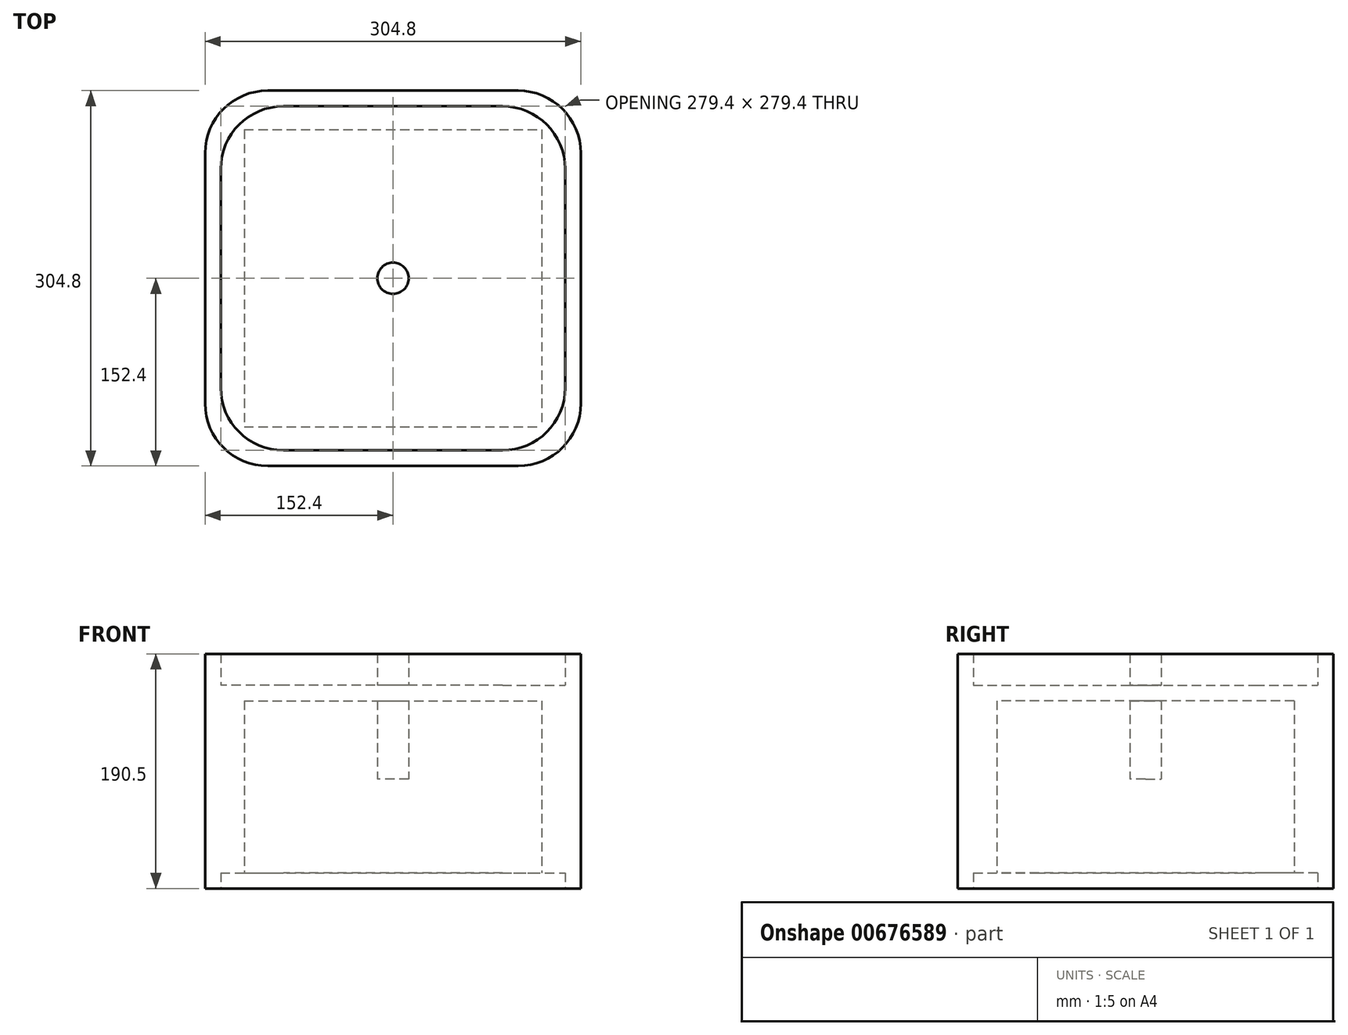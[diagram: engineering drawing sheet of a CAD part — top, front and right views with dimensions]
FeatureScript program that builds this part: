
annotation { "Feature Type Name" : "Feature", "Feature Type Description" : "" }
export const myFeature = defineFeature(function(context is Context, id is Id, definition is map)
    precondition{}
    {
        {
            var Q0;
            Q0=qCreatedBy(makeId("Top.planeOp"),FACE);
            var sketch = newSketch(context, id + "F0", { "sketchPlane" : qUnion([Q0])});
            skPoint(sketch, "E0.middle", {"position": v(0, 0) * mm});
            skLineSegment(sketch, "E1.bottom", {"start": v(139.7, -139.7) * mm, "end": v(-139.7, -139.7) * mm});
            skLineSegment(sketch, "E1.top", {"start": v(139.7, 139.7) * mm, "end": v(-139.7, 139.7) * mm});
            skLineSegment(sketch, "E1.left", {"start": v(139.7, -139.7) * mm, "end": v(139.7, 139.7) * mm});
            skLineSegment(sketch, "E1.right", {"start": v(-139.7, -139.7) * mm, "end": v(-139.7, 139.7) * mm});
            skCircle(sketch, "E2", {"center": v(0, 0) * mm, "radius": 12.7 * mm});
            skLineSegment(sketch, "E3.bottom", {"start": v(152.4, -152.4) * mm, "end": v(-152.4, -152.4) * mm});
            skLineSegment(sketch, "E3.top", {"start": v(152.4, 152.4) * mm, "end": v(-152.4, 152.4) * mm});
            skLineSegment(sketch, "E3.left", {"start": v(152.4, -152.4) * mm, "end": v(152.4, 152.4) * mm});
            skLineSegment(sketch, "E3.right", {"start": v(-152.4, -152.4) * mm, "end": v(-152.4, 152.4) * mm});
            skSolve(sketch);
        }
        {
            var Q0;
            Q0=makeQuery(id+"F0.imprint","IMPRINT",FACE,{"disambiguationData":[TD([[makeQuery(id+"F0.imprint","IMPRINT",EDGE,{"derivedFrom":sQuery(id+"F0.wireOp",EDGE,"E1.bottom")}),-1.0]])]});
            extrude(context, id + "F1", {"entities" : qUnion([Q0]), "endBound" : BoundingType.SYMMETRIC, "depth" : 152.4 * mm, "offsetDistance" : 25.4 * mm});
        }
        {
            var Q0;
            Q0=makeQuery(id+"F0.imprint","IMPRINT",FACE,{"disambiguationData":[TD([[makeQuery(id+"F0.imprint","IMPRINT",EDGE,{"derivedFrom":sQuery(id+"F0.wireOp",EDGE,"E1.bottom")}),1.0]])]});
            extrude(context, id + "F2", {"entities" : qUnion([Q0]), "operationType" : NewBodyOperationType.ADD, "depth" : 101.6 * mm, "offsetDistance" : 25.4 * mm, "hasSecondDirection" : true, "secondDirectionOppositeDirection" : true, "secondDirectionDepth" : 88.9 * mm});
        }
        {
            var Q0;
            Q0=makeQuery(id+"F2.opExtrude","SWEPT_EDGE",EDGE,{"disambiguationData":[OSD([sQuery(id+"F0.wireOp",EDGE,"E3.bottom"),sQuery(id+"F0.wireOp",EDGE,"E3.left")])]});
            var Q1;
            Q1=makeQuery(id+"F2.opExtrude","SWEPT_EDGE",EDGE,{"disambiguationData":[OSD([sQuery(id+"F0.wireOp",EDGE,"E3.top"),sQuery(id+"F0.wireOp",EDGE,"E3.left")])]});
            var Q2;
            Q2=makeQuery(id+"F2.opExtrude","SWEPT_EDGE",EDGE,{"disambiguationData":[OSD([sQuery(id+"F0.wireOp",EDGE,"E3.top"),sQuery(id+"F0.wireOp",EDGE,"E3.right")])]});
            var Q3;
            Q3=makeQuery(id+"F2.opExtrude","SWEPT_EDGE",EDGE,{"disambiguationData":[OSD([sQuery(id+"F0.wireOp",EDGE,"E3.bottom"),sQuery(id+"F0.wireOp",EDGE,"E3.right")])]});
            var Q4;
            {var subQ0=sQuery(id+"F0.wireOp",EDGE,"E1.right");var subQ1=sQuery(id+"F0.wireOp",EDGE,"E1.left");var subQ2=sQuery(id+"F0.wireOp",EDGE,"E1.top");var subQ3=sQuery(id+"F0.wireOp",EDGE,"E1.bottom");Q4=makeQuery(id+"F2.boolean.opBoolean","SPLIT",EDGE,{"disambiguationData":[TD([makeQuery(id+"F1.opExtrude","CAP_FACE",FACE,{"disambiguationData":[OSD([subQ3,subQ2,subQ1,subQ0,sQuery(id+"F0.wireOp",EDGE,"E2")])],"isStart":false})])],"derivedFrom":makeQuery(id+"F2.opExtrude","SWEPT_EDGE",EDGE,{"disambiguationData":[OSD([subQ3,subQ0])]})});}
            var Q5;
            {var subQ0=sQuery(id+"F0.wireOp",EDGE,"E1.right");var subQ1=sQuery(id+"F0.wireOp",EDGE,"E1.left");var subQ2=sQuery(id+"F0.wireOp",EDGE,"E1.top");var subQ3=sQuery(id+"F0.wireOp",EDGE,"E1.bottom");Q5=makeQuery(id+"F2.boolean.opBoolean","SPLIT",EDGE,{"disambiguationData":[TD([makeQuery(id+"F1.opExtrude","CAP_FACE",FACE,{"disambiguationData":[OSD([subQ3,subQ2,subQ1,subQ0,sQuery(id+"F0.wireOp",EDGE,"E2")])],"isStart":false})])],"derivedFrom":makeQuery(id+"F2.opExtrude","SWEPT_EDGE",EDGE,{"disambiguationData":[OSD([subQ2,subQ0])]})});}
            var Q6;
            {var subQ0=sQuery(id+"F0.wireOp",EDGE,"E1.right");var subQ1=sQuery(id+"F0.wireOp",EDGE,"E1.left");var subQ2=sQuery(id+"F0.wireOp",EDGE,"E1.top");var subQ3=sQuery(id+"F0.wireOp",EDGE,"E1.bottom");Q6=makeQuery(id+"F2.boolean.opBoolean","SPLIT",EDGE,{"disambiguationData":[TD([makeQuery(id+"F1.opExtrude","CAP_FACE",FACE,{"disambiguationData":[OSD([subQ3,subQ2,subQ1,subQ0,sQuery(id+"F0.wireOp",EDGE,"E2")])],"isStart":false})])],"derivedFrom":makeQuery(id+"F2.opExtrude","SWEPT_EDGE",EDGE,{"disambiguationData":[OSD([subQ2,subQ1])]})});}
            var Q7;
            {var subQ0=sQuery(id+"F0.wireOp",EDGE,"E1.right");var subQ1=sQuery(id+"F0.wireOp",EDGE,"E1.left");var subQ2=sQuery(id+"F0.wireOp",EDGE,"E1.top");var subQ3=sQuery(id+"F0.wireOp",EDGE,"E1.bottom");Q7=makeQuery(id+"F2.boolean.opBoolean","SPLIT",EDGE,{"disambiguationData":[TD([makeQuery(id+"F1.opExtrude","CAP_FACE",FACE,{"disambiguationData":[OSD([subQ3,subQ2,subQ1,subQ0,sQuery(id+"F0.wireOp",EDGE,"E2")])],"isStart":false})])],"derivedFrom":makeQuery(id+"F2.opExtrude","SWEPT_EDGE",EDGE,{"disambiguationData":[OSD([subQ3,subQ1])]})});}
            var Q8;
            {var subQ0=sQuery(id+"F0.wireOp",EDGE,"E1.right");var subQ1=sQuery(id+"F0.wireOp",EDGE,"E1.left");var subQ2=sQuery(id+"F0.wireOp",EDGE,"E1.top");var subQ3=sQuery(id+"F0.wireOp",EDGE,"E1.bottom");Q8=makeQuery(id+"F2.boolean.opBoolean","SPLIT",EDGE,{"disambiguationData":[TD([makeQuery(id+"F1.opExtrude","CAP_FACE",FACE,{"disambiguationData":[OSD([subQ3,subQ2,subQ1,subQ0,sQuery(id+"F0.wireOp",EDGE,"E2")])],"isStart":true})])],"derivedFrom":makeQuery(id+"F2.opExtrude","SWEPT_EDGE",EDGE,{"disambiguationData":[OSD([subQ2,subQ0])]})});}
            var Q9;
            {var subQ0=sQuery(id+"F0.wireOp",EDGE,"E1.right");var subQ1=sQuery(id+"F0.wireOp",EDGE,"E1.left");var subQ2=sQuery(id+"F0.wireOp",EDGE,"E1.top");var subQ3=sQuery(id+"F0.wireOp",EDGE,"E1.bottom");Q9=makeQuery(id+"F2.boolean.opBoolean","SPLIT",EDGE,{"disambiguationData":[TD([makeQuery(id+"F1.opExtrude","CAP_FACE",FACE,{"disambiguationData":[OSD([subQ3,subQ2,subQ1,subQ0,sQuery(id+"F0.wireOp",EDGE,"E2")])],"isStart":true})])],"derivedFrom":makeQuery(id+"F2.opExtrude","SWEPT_EDGE",EDGE,{"disambiguationData":[OSD([subQ3,subQ0])]})});}
            var Q10;
            {var subQ0=sQuery(id+"F0.wireOp",EDGE,"E1.right");var subQ1=sQuery(id+"F0.wireOp",EDGE,"E1.left");var subQ2=sQuery(id+"F0.wireOp",EDGE,"E1.top");var subQ3=sQuery(id+"F0.wireOp",EDGE,"E1.bottom");Q10=makeQuery(id+"F2.boolean.opBoolean","SPLIT",EDGE,{"disambiguationData":[TD([makeQuery(id+"F1.opExtrude","CAP_FACE",FACE,{"disambiguationData":[OSD([subQ3,subQ2,subQ1,subQ0,sQuery(id+"F0.wireOp",EDGE,"E2")])],"isStart":true})])],"derivedFrom":makeQuery(id+"F2.opExtrude","SWEPT_EDGE",EDGE,{"disambiguationData":[OSD([subQ2,subQ1])]})});}
            var Q11;
            {var subQ0=sQuery(id+"F0.wireOp",EDGE,"E1.right");var subQ1=sQuery(id+"F0.wireOp",EDGE,"E1.left");var subQ2=sQuery(id+"F0.wireOp",EDGE,"E1.top");var subQ3=sQuery(id+"F0.wireOp",EDGE,"E1.bottom");Q11=makeQuery(id+"F2.boolean.opBoolean","SPLIT",EDGE,{"disambiguationData":[TD([makeQuery(id+"F1.opExtrude","CAP_FACE",FACE,{"disambiguationData":[OSD([subQ3,subQ2,subQ1,subQ0,sQuery(id+"F0.wireOp",EDGE,"E2")])],"isStart":true})])],"derivedFrom":makeQuery(id+"F2.opExtrude","SWEPT_EDGE",EDGE,{"disambiguationData":[OSD([subQ3,subQ1])]})});}
            fillet(context, id + "F3", {"entities" : qUnion([Q0, Q1, Q2, Q3, Q4, Q5, Q6, Q7, Q8, Q9, Q10, Q11]), "radius" : 50.8 * mm, "tangentPropagation" : true, "allowEdgeOverflow" : false});
        }
        {
            var Q0;
            Q0=makeQuery(id+"F1.opExtrude","CAP_FACE",FACE,{"disambiguationData":[OSD([sQuery(id+"F0.wireOp",EDGE,"E1.bottom"),sQuery(id+"F0.wireOp",EDGE,"E1.top"),sQuery(id+"F0.wireOp",EDGE,"E1.left"),sQuery(id+"F0.wireOp",EDGE,"E1.right"),sQuery(id+"F0.wireOp",EDGE,"E2")])],"isStart":true});
            var sketch = newSketch(context, id + "F4", { "sketchPlane" : qUnion([Q0])});
            skLineSegment(sketch, "E4.bottom", {"start": v(-120.65, -120.65) * mm, "end": v(120.65, -120.65) * mm});
            skLineSegment(sketch, "E4.top", {"start": v(-120.65, 120.65) * mm, "end": v(120.65, 120.65) * mm});
            skLineSegment(sketch, "E4.left", {"start": v(-120.65, -120.65) * mm, "end": v(-120.65, 120.65) * mm});
            skLineSegment(sketch, "E4.right", {"start": v(120.65, -120.65) * mm, "end": v(120.65, 120.65) * mm});
            skPoint(sketch, "E4.middle", {"position": v(0, 0) * mm});
            skSolve(sketch);
        }
        {
            var Q0;
            Q0 = qSketchRegion(id + "F4", true);
            extrude(context, id + "F5", {"entities" : qUnion([Q0]), "operationType" : NewBodyOperationType.REMOVE, "oppositeDirection" : true, "depth" : 139.7 * mm, "offsetDistance" : 25.4 * mm});
        }
        {
            var Q0;
            Q0=makeQuery(id+"F0.imprint","IMPRINT",FACE,{"disambiguationData":[TD([[makeQuery(id+"F0.imprint","IMPRINT",EDGE,{"derivedFrom":sQuery(id+"F0.wireOp",EDGE,"E2")}),1.0]])]});
            extrude(context, id + "F6", {"entities" : qUnion([Q0]), "operationType" : NewBodyOperationType.ADD, "depth" : 101.6 * mm, "offsetDistance" : 25.4 * mm});
        }
    });
